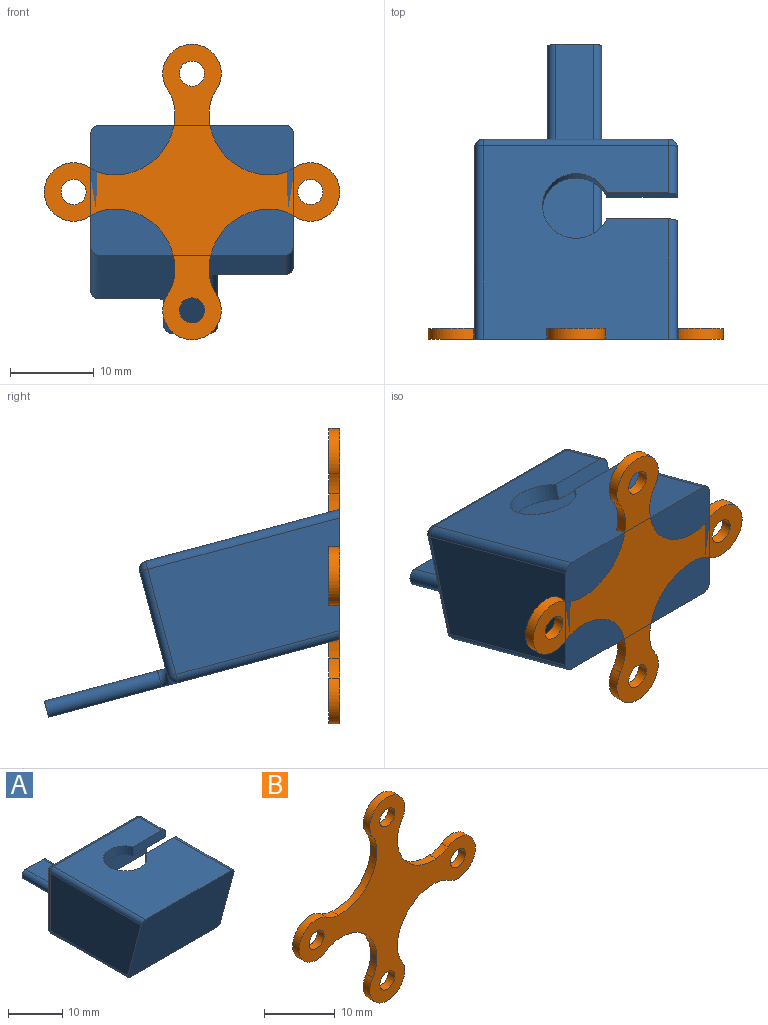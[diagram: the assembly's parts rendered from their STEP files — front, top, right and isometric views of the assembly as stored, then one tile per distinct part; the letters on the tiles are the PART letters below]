
ASSEMBLY  parts=2 mates=1
PART A: 34 faces, bbox 24.3x40.1x15.1 mm
  f0: plane 22.31x13.11mm, normal (0,1,0), area 201.2mm2, adj f14,f15,f21,f23,f24,f30,f31
  f1: plane 14.63x13mm, normal (1,0,0), area 89.8mm2, adj f3,f5,f12,f13,f16,f17,f27,f28
  f2: plane 23.73x13mm, normal (-1,0,0), area 285.9mm2, adj f17,f19,f20,f21
  f3: plane 22.2x15mm, normal (0,0,-1), area 256.5mm2, adj f1,f4,f6,f9,f10,f11,f12,f16
  f4: plane 15x11mm, normal (1,0,0), area 165mm2, adj f3,f5,f9,f16
  f5: plane 32x22.2mm, normal (0,0,1), area 311.3mm2, adj f1,f4,f9,f13,f15,f16,f18,f29
  f6: plane 7x5.9mm, normal (1,0,0), area 11.9mm2, adj f3,f9,f10,f14,f24,f26
  f7: plane 24x22.2mm, normal (0,0,1), area 459.5mm2, adj f10,f11,f12,f17,f20,f23,f26,f28
  f8: plane 35.98x22.2mm, normal (0,0,-1), area 417.4mm2, adj f13,f17,f18,f19,f27,f29,f30,f31
  f9: plane 22.2x11mm, normal (0,-1,0), area 166.7mm2, adj f3,f4,f5,f6,f14,f15
  f10: plane 8.43x2mm, normal (0,-1,0), area 16.7mm2, adj f3,f6,f7,f11,f26
  f11: cylinder r=4mm len=8mm, axis (0,0,1), area 43.7mm2, adj f3,f7,f10,f12
  f12: plane 8.43x2mm, normal (0,1,0), area 16.7mm2, adj f1,f3,f7,f11,f28
  f13: plane 10x2mm, normal (0,1,0), area 18.2mm2, adj f1,f5,f8,f27,f33
  f14: plane 15.5x2mm, normal (0,0,-1), area 30.8mm2, adj f0,f6,f9,f15,f24
  f15: plane 5.26x2.07mm, normal (1,0,0), area 10mm2, adj f0,f5,f9,f14,f30
  f16: plane 22.2x11mm, normal (0,1,0), area 244.2mm2, adj f1,f3,f4,f5
  f17: plane 24.31x15.11mm, normal (0,-0.97,-0.26), area 374.9mm2, adj f1,f2,f7,f8,f19,f20,f27,f28
  f18: plane 6.5x2mm, normal (0,1,0), area 12.1mm2, adj f5,f8,f29,f33
  f19: cylinder r=1mm len=20.25mm, axis (0,1,0), area 31.6mm2, adj f2,f8,f17,f32
  f20: cylinder r=1mm len=24mm, axis (0,-1,0), area 37.5mm2, adj f2,f7,f17,f22
  f21: cylinder r=1mm len=13mm, axis (0,0,-1), area 20.4mm2, adj f0,f2,f22,f32
  f22: sphere r=1mm, area 1.6mm2, adj f20,f21,f23
  f23: cylinder r=1mm len=22.2mm, axis (-1,0,0), area 34.9mm2, adj f0,f7,f22,f25
  f24: cylinder r=1mm len=7mm, axis (0,0,1), area 11mm2, adj f0,f6,f14,f25
  f25: sphere r=1mm, area 1.6mm2, adj f23,f24,f26
  f26: cylinder r=1mm len=5.9mm, axis (0,-1,0), area 9.3mm2, adj f6,f7,f10,f25
  f27: cylinder r=1mm len=9.25mm, axis (0,1,0), area 14.3mm2, adj f1,f8,f13,f17
  f28: cylinder r=1mm len=14.9mm, axis (0,-1,0), area 23.2mm2, adj f1,f7,f12,f17
  f29: cylinder r=1mm len=14mm, axis (0,-1,0), area 44mm2, adj f5,f8,f18,f30
  f30: torus R=2mm, axis (0,0,-1), area 5.6mm2, adj f0,f5,f8,f15,f29,f31
  f31: cylinder r=1mm len=6.7mm, axis (1,0,0), area 10.5mm2, adj f0,f8,f30,f32
  f32: sphere r=1mm, area 1.6mm2, adj f19,f21,f31
  f33: cylinder r=1mm len=27mm, axis (0,1,0), area 84.8mm2, adj f5,f8,f13,f18
PART B: 22 faces, bbox 35.3x1.3x35.3 mm
  f0: cylinder r=5mm len=2.39mm, axis (0,1,0), area 3.3mm2, adj f1,f19,f20,f21
  f1: cylinder r=3.5mm len=7mm, axis (0,1,0), area 19.7mm2, adj f0,f2,f20,f21
  f2: cylinder r=5mm len=2.39mm, axis (0,1,0), area 3.3mm2, adj f1,f3,f20,f21
  f3: cylinder r=7.18mm len=7.75mm, axis (0,1,0), area 16.1mm2, adj f2,f4,f20,f21
  f4: cylinder r=5mm len=2.39mm, axis (0,1,0), area 3.3mm2, adj f3,f5,f20,f21
  f5: cylinder r=3.5mm len=7mm, axis (0,1,0), area 19.7mm2, adj f4,f6,f20,f21
  f6: cylinder r=5mm len=2.39mm, axis (0,1,0), area 3.3mm2, adj f5,f7,f20,f21
  f7: cylinder r=7.18mm len=7.75mm, axis (0,1,0), area 16.1mm2, adj f6,f8,f20,f21
  f8: cylinder r=5mm len=2.39mm, axis (0,1,0), area 3.3mm2, adj f7,f9,f20,f21
  f9: cylinder r=3.5mm len=7mm, axis (0,1,0), area 19.7mm2, adj f8,f10,f20,f21
  f10: cylinder r=5mm len=2.39mm, axis (0,1,0), area 3.3mm2, adj f9,f11,f20,f21
  f11: cylinder r=7.18mm len=7.75mm, axis (0,1,0), area 16.1mm2, adj f10,f12,f20,f21
  f12: cylinder r=5mm len=2.39mm, axis (0,1,0), area 3.3mm2, adj f11,f13,f20,f21
  f13: cylinder r=3.5mm len=7mm, axis (0,1,0), area 19.7mm2, adj f12,f14,f20,f21
  f14: cylinder r=5mm len=2.39mm, axis (0,1,0), area 3.3mm2, adj f13,f19,f20,f21
  f15: cylinder r=1.5mm len=3mm, axis (0,1,0), area 12.3mm2, adj f20,f21
  f16: cylinder r=1.5mm len=3mm, axis (0,1,0), area 12.3mm2, adj f20,f21
  f17: cylinder r=1.5mm len=3mm, axis (0,1,0), area 12.3mm2, adj f20,f21
  f18: cylinder r=1.5mm len=3mm, axis (0,1,0), area 12.3mm2, adj f20,f21
  f19: cylinder r=7.18mm len=7.75mm, axis (0,1,0), area 16.1mm2, adj f0,f14,f20,f21
  f20: plane 35.28x35.28mm, normal (0,-1,0), area 333.8mm2, adj f0,f1,f2,f3,f4,f5,f6,f7
  f21: plane 35.28x35.28mm, normal (0,1,0), area 333.8mm2, adj f0,f1,f2,f3,f4,f5,f6,f7
PLACE A rot(axis=(-1,0,0),15deg) t=(0,21.37,26.26)mm
PLACE B t=(0,0.46,32)mm
MATE planar A.f17 <-> B.f20  axis (0,-1,0) through (0,-0.84,32.21)mm
